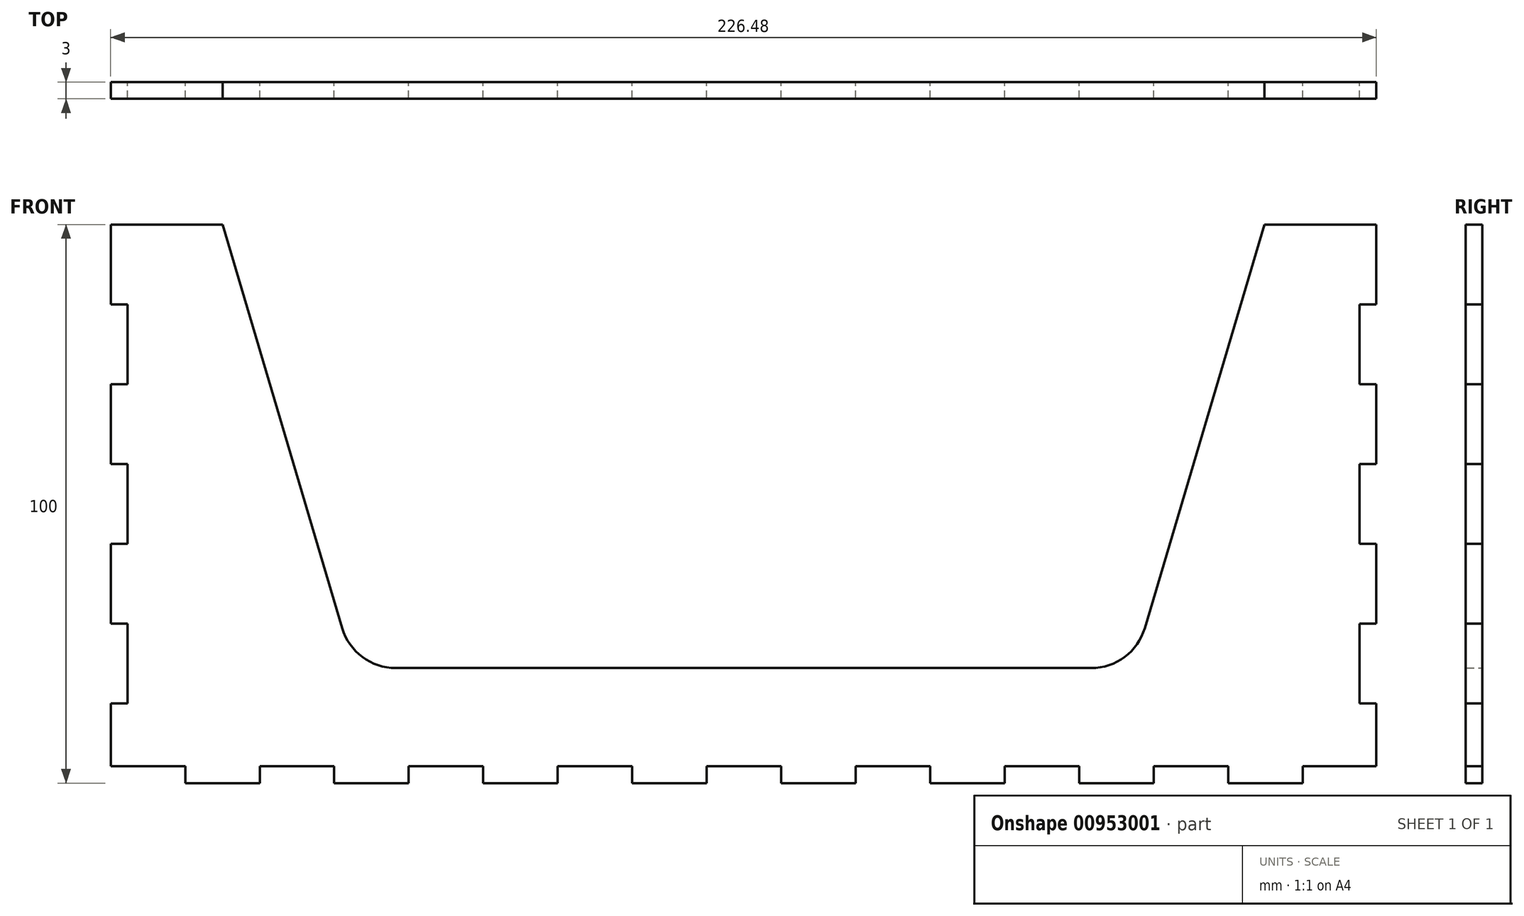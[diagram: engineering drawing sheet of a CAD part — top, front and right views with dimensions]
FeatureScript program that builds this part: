
annotation { "Feature Type Name" : "Feature", "Feature Type Description" : "" }
export const myFeature = defineFeature(function(context is Context, id is Id, definition is map)
    precondition{}
    {
        {
            var Q0;
            Q0=qCreatedBy(makeId("Front.planeOp"),FACE);
            var sketch = newSketch(context, id + "F0", { "sketchPlane" : qUnion([Q0])});
            skLineSegment(sketch, "E0.bottom", {"start": v(73.43, -50) * mm, "end": v(60.1, -50) * mm});
            skLineSegment(sketch, "E0.right", {"start": v(-113.24, -47) * mm, "end": v(-113.24, -35.71) * mm});
            skLineSegment(sketch, "E1", {"start": v(-113.24, -47) * mm, "end": v(-99.9, -47) * mm});
            skLineSegment(sketch, "E2", {"start": v(-99.9, -47) * mm, "end": v(-99.9, -50) * mm});
            skLineSegment(sketch, "E3", {"start": v(-86.57, -47) * mm, "end": v(-86.57, -50) * mm});
            skLineSegment(sketch, "E4", {"start": v(-59.9, -47) * mm, "end": v(-59.9, -50) * mm});
            skLineSegment(sketch, "E5", {"start": v(-33.24, -47) * mm, "end": v(-33.24, -50) * mm});
            skLineSegment(sketch, "E6", {"start": v(-19.9, -47) * mm, "end": v(-19.9, -50) * mm});
            skLineSegment(sketch, "E7", {"start": v(6.76, -47) * mm, "end": v(6.76, -50) * mm});
            skLineSegment(sketch, "E8", {"start": v(33.43, -47) * mm, "end": v(33.43, -50) * mm});
            skLineSegment(sketch, "E9", {"start": v(46.76, -47) * mm, "end": v(46.76, -50) * mm});
            skLineSegment(sketch, "E10", {"start": v(-73.24, -47) * mm, "end": v(-73.24, -50) * mm});
            skLineSegment(sketch, "E11", {"start": v(-46.57, -47) * mm, "end": v(-46.57, -50) * mm});
            skLineSegment(sketch, "E12", {"start": v(-6.57, -47) * mm, "end": v(-6.57, -50) * mm});
            skLineSegment(sketch, "E13", {"start": v(20.1, -47) * mm, "end": v(20.1, -50) * mm});
            skLineSegment(sketch, "E14", {"start": v(60.1, -47) * mm, "end": v(60.1, -50) * mm});
            skLineSegment(sketch, "E15", {"start": v(73.43, -47) * mm, "end": v(73.43, -50) * mm});
            skPoint(sketch, "E16.orphan", {"position": v(-113.24, -50) * mm});
            skLineSegment(sketch, "E17.trimOffspring", {"start": v(-86.57, -47) * mm, "end": v(-73.24, -47) * mm});
            skLineSegment(sketch, "E18.trimOffspring", {"start": v(-86.57, -50) * mm, "end": v(-99.9, -50) * mm});
            skLineSegment(sketch, "E19.trimOffspring", {"start": v(-59.9, -47) * mm, "end": v(-46.57, -47) * mm});
            skLineSegment(sketch, "E20.trimOffspring", {"start": v(-59.9, -50) * mm, "end": v(-73.24, -50) * mm});
            skLineSegment(sketch, "E21.trimOffspring", {"start": v(-33.24, -47) * mm, "end": v(-19.9, -47) * mm});
            skLineSegment(sketch, "E22.trimOffspring", {"start": v(-33.24, -50) * mm, "end": v(-46.57, -50) * mm});
            skLineSegment(sketch, "E23.trimOffspring", {"start": v(-6.57, -47) * mm, "end": v(6.76, -47) * mm});
            skLineSegment(sketch, "E24.trimOffspring", {"start": v(-6.57, -50) * mm, "end": v(-19.9, -50) * mm});
            skLineSegment(sketch, "E25.trimOffspring", {"start": v(20.1, -47) * mm, "end": v(33.43, -47) * mm});
            skLineSegment(sketch, "E26.trimOffspring", {"start": v(20.1, -50) * mm, "end": v(6.76, -50) * mm});
            skLineSegment(sketch, "E27.trimOffspring", {"start": v(46.76, -47) * mm, "end": v(60.1, -47) * mm});
            skLineSegment(sketch, "E28.trimOffspring", {"start": v(46.76, -50) * mm, "end": v(33.43, -50) * mm});
            skLineSegment(sketch, "E29.trimOffspring", {"start": v(73.43, -47) * mm, "end": v(86.76, -47) * mm});
            skPoint(sketch, "E30.orphan", {"position": v(86.76, -50) * mm});
            skLineSegment(sketch, "E31", {"start": v(-110.24, 35.71) * mm, "end": v(-110.24, 21.43) * mm});
            skLineSegment(sketch, "E32", {"start": v(-113.24, 35.71) * mm, "end": v(-110.24, 35.71) * mm});
            skLineSegment(sketch, "E33", {"start": v(-113.24, 21.43) * mm, "end": v(-110.24, 21.43) * mm});
            skLineSegment(sketch, "E34", {"start": v(-113.24, 7.14) * mm, "end": v(-110.24, 7.14) * mm});
            skLineSegment(sketch, "E35", {"start": v(-113.24, -7.14) * mm, "end": v(-110.24, -7.14) * mm});
            skLineSegment(sketch, "E36", {"start": v(-113.24, -21.43) * mm, "end": v(-110.24, -21.43) * mm});
            skLineSegment(sketch, "E37", {"start": v(-113.24, -35.71) * mm, "end": v(-110.24, -35.71) * mm});
            skLineSegment(sketch, "E38.trimOffspring", {"start": v(-113.24, 35.71) * mm, "end": v(-113.24, 50) * mm});
            skLineSegment(sketch, "E39.trimOffspring", {"start": v(-110.24, 7.14) * mm, "end": v(-110.24, -7.14) * mm});
            skLineSegment(sketch, "E40.trimOffspring", {"start": v(-113.24, 7.14) * mm, "end": v(-113.24, 21.43) * mm});
            skLineSegment(sketch, "E41.trimOffspring", {"start": v(-110.24, -21.43) * mm, "end": v(-110.24, -35.71) * mm});
            skLineSegment(sketch, "E42.trimOffspring", {"start": v(-113.24, -21.43) * mm, "end": v(-113.24, -7.14) * mm});
            skPoint(sketch, "E43.MirrorP", {"position": v(100, -50) * mm});
            skLineSegment(sketch, "E44.trimOffspring", {"start": v(-93.24, 50) * mm, "end": v(-113.24, 50) * mm});
            skPoint(sketch, "E45.MirrorCS.start.orphan", {"position": v(100, -47) * mm});
            skLineSegment(sketch, "E46.bottom", {"start": v(100.1, -50) * mm, "end": v(86.76, -50) * mm});
            skLineSegment(sketch, "E47", {"start": v(86.76, -47) * mm, "end": v(86.76, -50) * mm});
            skLineSegment(sketch, "E48", {"start": v(100.1, -47) * mm, "end": v(100.1, -50) * mm});
            skLineSegment(sketch, "E49.trimOffspring", {"start": v(100.1, -47) * mm, "end": v(113.43, -47) * mm});
            skPoint(sketch, "E50.MirrorP", {"position": v(113.43, -50) * mm});
            skLineSegment(sketch, "E51.MirrorCS", {"start": v(113.24, 35.71) * mm, "end": v(110.24, 35.71) * mm});
            skLineSegment(sketch, "E52.MirrorCS", {"start": v(113.24, -7.14) * mm, "end": v(110.24, -7.14) * mm});
            skLineSegment(sketch, "E53.MirrorCS", {"start": v(113.24, -21.43) * mm, "end": v(110.24, -21.43) * mm});
            skLineSegment(sketch, "E54.MirrorCS", {"start": v(113.24, -35.71) * mm, "end": v(110.24, -35.71) * mm});
            skLineSegment(sketch, "E55.MirrorCS", {"start": v(113.24, 7.14) * mm, "end": v(110.24, 7.14) * mm});
            skLineSegment(sketch, "E56.MirrorCS", {"start": v(113.24, 21.43) * mm, "end": v(110.24, 21.43) * mm});
            skLineSegment(sketch, "E57.MirrorCS", {"start": v(110.24, 7.14) * mm, "end": v(110.24, -7.14) * mm});
            skLineSegment(sketch, "E58.MirrorCS", {"start": v(110.24, -21.43) * mm, "end": v(110.24, -35.71) * mm});
            skLineSegment(sketch, "E59.MirrorCS", {"start": v(110.24, 35.71) * mm, "end": v(110.24, 21.43) * mm});
            skLineSegment(sketch, "E60.MirrorCS", {"start": v(113.24, 35.71) * mm, "end": v(113.24, 50) * mm});
            skLineSegment(sketch, "E61.MirrorCS", {"start": v(113.24, -47) * mm, "end": v(113.24, -35.71) * mm});
            skLineSegment(sketch, "E62.MirrorCS", {"start": v(113.24, 7.14) * mm, "end": v(113.24, 21.43) * mm});
            skLineSegment(sketch, "E63.MirrorCS", {"start": v(113.24, -21.43) * mm, "end": v(113.24, -7.14) * mm});
            skLineSegment(sketch, "E64.MirrorCS", {"start": v(62.22, -29.41) * mm, "end": v(0, -29.41) * mm});
            skLineSegment(sketch, "E65.MirrorCS", {"start": v(93.24, 50) * mm, "end": v(71.81, -22.25) * mm});
            skLineSegment(sketch, "E66", {"start": v(93.24, 50) * mm, "end": v(113.24, 50) * mm});
            skPoint(sketch, "E67.visualSharp", {"position": v(69.69, -29.41) * mm});
            skArc(sketch, "E67.filletArc", {"start": v(62.22, -29.41) * mm, "mid": v(68.2, -27.42) * mm, "end": v(71.81, -22.25) * mm});
            skPoint(sketch, "E68.end.orphan", {"position": v(0, -29.41) * mm});
            skArc(sketch, "E69.MirrorCS", {"start": v(-62.22, -29.41) * mm, "mid": v(-68.2, -27.42) * mm, "end": v(-71.81, -22.25) * mm});
            skLineSegment(sketch, "E70.MirrorCS", {"start": v(-62.22, -29.41) * mm, "end": v(0, -29.41) * mm});
            skLineSegment(sketch, "E71.MirrorCS", {"start": v(-93.24, 50) * mm, "end": v(-71.81, -22.25) * mm});
            skPoint(sketch, "E72.MirrorP", {"position": v(-69.69, -29.41) * mm});
            skSolve(sketch);
        }
        {
            var Q0;
            Q0=makeQuery(id+"F0.imprint","IMPRINT",FACE,{"disambiguationData":[TD([[makeQuery(id+"F0.imprint","IMPRINT",EDGE,{"derivedFrom":sQuery(id+"F0.wireOp",EDGE,"E0.bottom")}),-1.0]])]});
            extrude(context, id + "F1", {"entities" : qUnion([Q0]), "depth" : 3 * mm, "offsetDistance" : 25 * mm});
        }
    });
